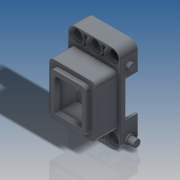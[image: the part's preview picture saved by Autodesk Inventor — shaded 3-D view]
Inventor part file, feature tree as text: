
AUTODESK INVENTOR PART (.ipt)
format: ipt  version: 2016 SP2 (Build 200236200, 236)  size: 495,616 bytes
history: native  units: in
note: dims shown in document units (in); Inventor stores cm internally (conversion verified against a paired STEP export)
features: extrude x13, sketch x3, mirror x1, fillet x1
ambient origin geometry x8: Origin, YZ Plane, XZ Plane, XY Plane, X Axis, Y Axis, Z Axis, Center Point
bodies: Solid1 (feature_tree)
feature tree (18):
  sketch  "Sketch2"  dims[d0=0.1417in d2=0.189in]
  extrude  "Extrusion1"  Depth=0.189in
  extrude  "Extrusion2"  Depth=0.315in
  extrude  "Extrusion3"  Depth=0.0157in
  extrude  "Extrusion4"  Depth=0.0787in
  extrude  "Extrusion5"  Depth=0.0157in
  sketch  "Sketch3"  dims[d3=0.2441in d4=0.315in]
  extrude  "Extrusion6"  Depth=0.0157in
  extrude  "Extrusion7"  Depth=0.9134in
  extrude  "Extrusion8"  Depth=0.4724in
  extrude  "Extrusion9"  Depth=0.6299in
  sketch  "Sketch4"  dims[d5=1.2598in d6=0.0378in d7=0.0787in d8=0.5732in d9=0.7559in d10=0.9134in d11=0.4724in d12=0.6299in d13=0.0945in d14=0.8189in d15=45.0deg d16=0.315in d17=0.0in d18=0.0315in d19=0.0in d20=0.252in d21=0.0in d22=0.378in d23=0.0in d24=0.4567in d25=0.0in d26=0.9764in d27=0.6299in d28=0.8189in d29=0.7244in d30=0.8189in d31=0.1732in d32=0.2441in d33=0.0315in d34=0.0in d35=0.2205in d36=0.0in d37=0.2677in d38=0.0in d39=0.6772in d40=0.0in d41=0.126in d42=0.1575in d43=0.1575in d44=1.1181in d45=0.063in d46=0.0in d47=0.0315in d48=0.0in d49=0.0315in d50=0.0in d51=0.1417in d52=0.0in d53=0.0039in d54=0.0157in]
  extrude  "Extrusion10"  Depth=0.0945in
  extrude  "Extrusion11"  Depth=0.8189in
  extrude  "Extrusion12"  TaperAngle=45.0deg  [1 undecoded]
  extrude  "Extrusion13"  Depth=0.315in
  mirror  "Mirror1"
  fillet  "Fillet1"  [1 undecoded]
note: 2 required parameter values undecoded (feature->parameter linkage not recoverable at this tier; creation-order binding heuristic only, values carry confidence <= 0.55)
